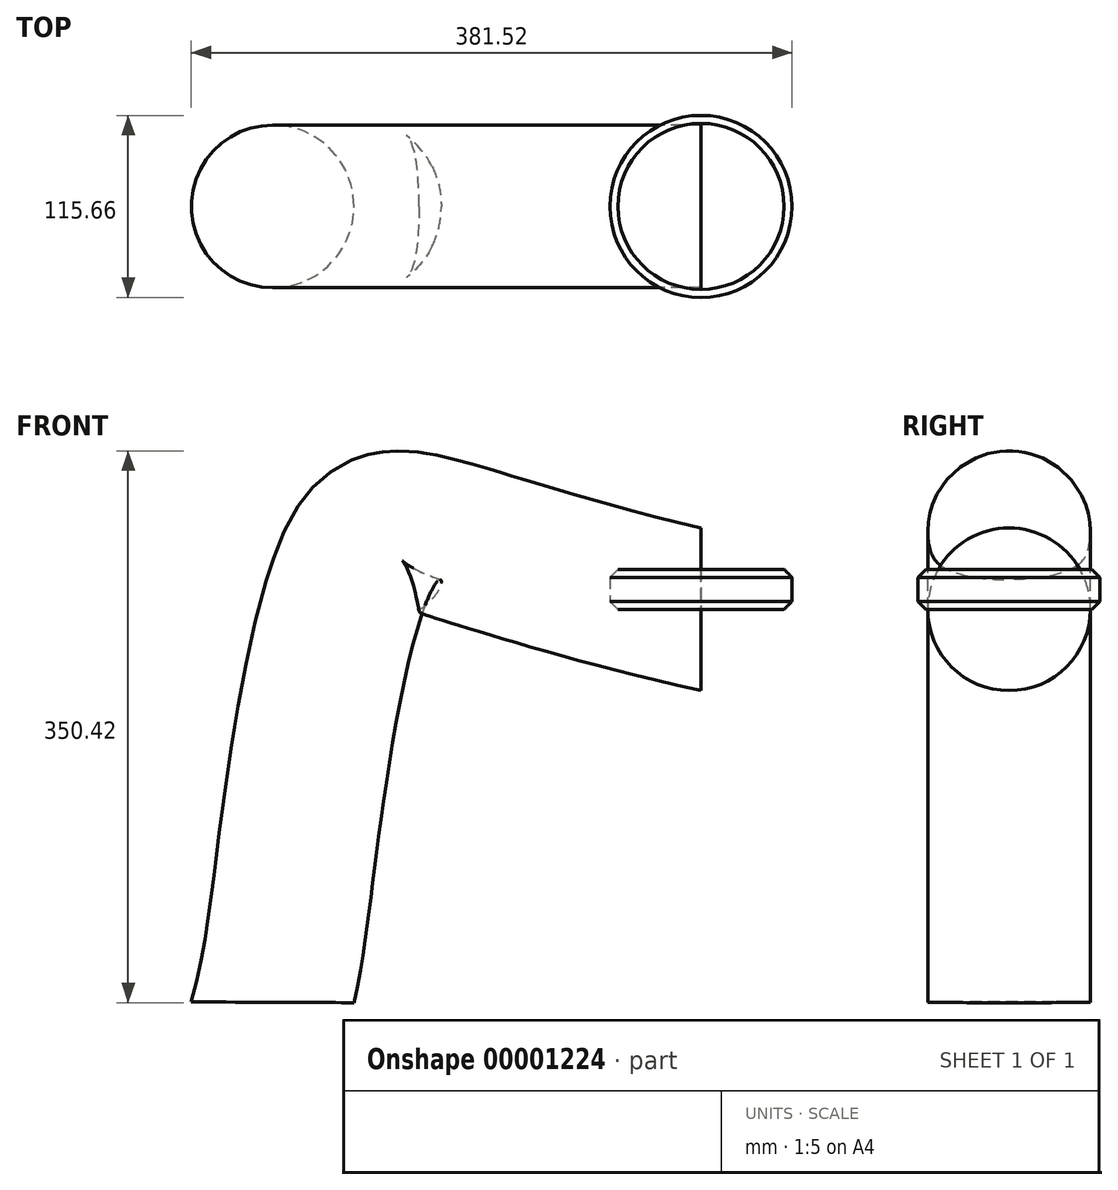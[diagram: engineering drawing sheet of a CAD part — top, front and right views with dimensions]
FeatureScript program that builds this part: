
annotation { "Feature Type Name" : "Feature", "Feature Type Description" : "" }
export const myFeature = defineFeature(function(context is Context, id is Id, definition is map)
    precondition{}
    {
        {
            var Q0;
            Q0=qCreatedBy(makeId("Top.planeOp"),FACE);
            var sketch = newSketch(context, id + "F0", { "sketchPlane" : qUnion([Q0])});
            skCircle(sketch, "E0", {"center": v(0, 0) * mm, "radius": 57.83 * mm});
            skSolve(sketch);
        }
        {
            var Q0;
            Q0=makeQuery(id+"F0.imprint","IMPRINT",FACE,{"disambiguationData":[TD([[makeQuery(id+"F0.imprint","IMPRINT",EDGE,{"derivedFrom":sQuery(id+"F0.wireOp",EDGE,"E0")}),1.0]])]});
            var Q1;
            Q1=sQuery(id+"F0.wireOp",EDGE,"E0");
            extrude(context, id + "F1", {"entities" : qUnion([Q0]), "surfaceEntities" : qUnion([Q1]), "depth" : 25.4 * mm});
        }
        {
            var Q0;
            Q0=makeQuery(id+"F1.opExtrude","CAP_FACE",FACE,{"disambiguationData":[OSD([sQuery(id+"F0.wireOp",EDGE,"E0")])],"isStart":false});
            var sketch = newSketch(context, id + "F2", { "sketchPlane" : qUnion([Q0])});
            skCircle(sketch, "E1", {"center": v(0, 0) * mm, "radius": 35.9 * mm});
            skCircle(sketch, "E2", {"center": v(0, 0) * mm, "radius": 23.53 * mm});
            skSolve(sketch);
        }
        {
            var Q0;
            Q0=makeQuery(id+"F1.opExtrude","CAP_EDGE",EDGE,{"disambiguationData":[OSD([sQuery(id+"F0.wireOp",EDGE,"E0")])],"isStart":false});
            var Q1;
            Q1=makeQuery(id+"F1.opExtrude","CAP_FACE",FACE,{"disambiguationData":[OSD([sQuery(id+"F0.wireOp",EDGE,"E0")])],"isStart":true});
            chamfer(context, id + "F7", {"entities" : qUnion([Q0, Q1]), "width" : 5.08 * mm, "tangentPropagation" : true});
        }
        {
            var Q0;
            Q0=sQuery(id+"F2.wireOp",EDGE,"E1");
            extrude(context, id + "F3", {"bodyType" : ToolBodyType.SURFACE, "surfaceEntities" : qUnion([Q0]), "endBound" : BoundingType.SYMMETRIC, "depth" : 414.76 * mm});
        }
        {
            var Q0;
            Q0=qCreatedBy(makeId("Front.planeOp"),FACE);
            var sketch = newSketch(context, id + "F4", { "sketchPlane" : qUnion([Q0])});
            skFitSpline(sketch, "E3", {"points": [v(0, 0) * mm, v(-215.37, 34.13) * mm, v(-254.94, -140.15) * mm, v(-272.03, -249.62) * mm], "startDerivative": vector(-1319.3, 304.15) * mm, "endDerivative": vector(-99.58, -423.17) * mm});
            skSolve(sketch);
        }
        {
            var Q0;
            Q0=qCreatedBy(makeId("Right.planeOp"),FACE);
            var sketch = newSketch(context, id + "F5", { "sketchPlane" : qUnion([Q0])});
            skCircle(sketch, "E4", {"center": v(0, 0) * mm, "radius": 51.66 * mm});
            skSolve(sketch);
        }
        {
            var Q0;
            Q0 = qSketchRegion(id + "F5", true);
            var Q1;
            Q1 = qConstructionFilter(qBodyType(qCreatedBy(id + "F4" ,EDGE), BodyType.WIRE), ConstructionObject.NO);
            sweep(context, id + "F6", {"profiles" : qUnion([Q0]), "path" : qUnion([Q1])});
        }
    });
